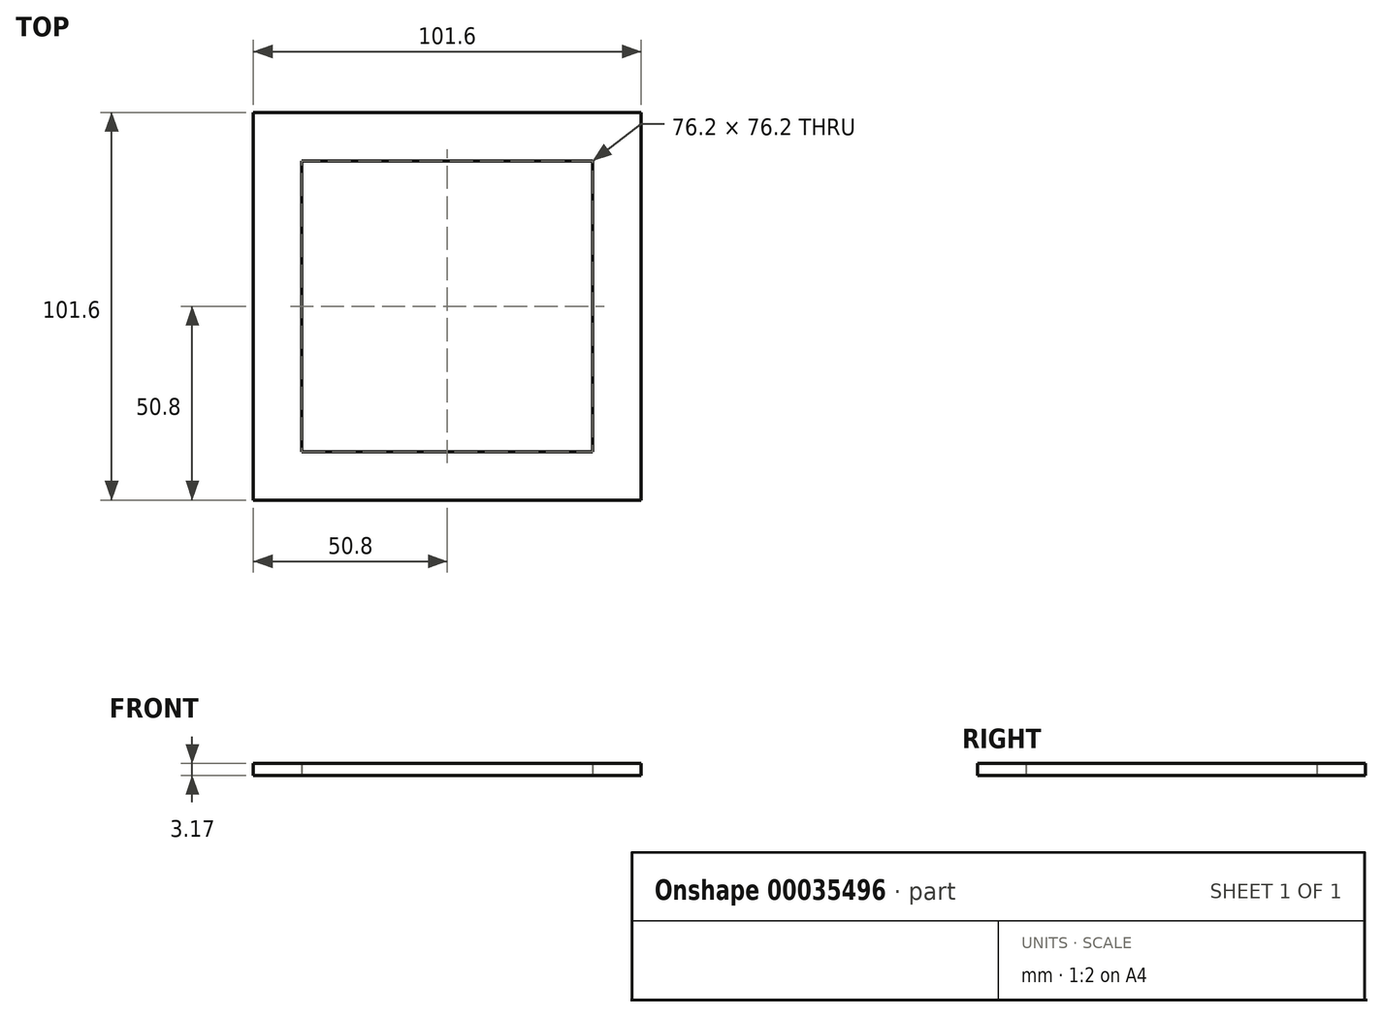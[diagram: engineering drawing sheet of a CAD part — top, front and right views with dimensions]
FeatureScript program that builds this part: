
annotation { "Feature Type Name" : "Feature", "Feature Type Description" : "" }
export const myFeature = defineFeature(function(context is Context, id is Id, definition is map)
    precondition{}
    {
        {
            var Q0;
            Q0=qCreatedBy(makeId("Top.planeOp"),FACE);
            var sketch = newSketch(context, id + "F0", { "sketchPlane" : qUnion([Q0])});
            skLineSegment(sketch, "E0.rect.bottom", {"start": v(-50.8, 50.8) * mm, "end": v(50.8, 50.8) * mm});
            skLineSegment(sketch, "E0.rect.top", {"start": v(-50.8, -50.8) * mm, "end": v(50.8, -50.8) * mm});
            skLineSegment(sketch, "E0.rect.left", {"start": v(-50.8, 50.8) * mm, "end": v(-50.8, -50.8) * mm});
            skLineSegment(sketch, "E0.rect.right", {"start": v(50.8, 50.8) * mm, "end": v(50.8, -50.8) * mm});
            skPoint(sketch, "E0.rect.middle", {"position": v(0, 0) * mm});
            skLineSegment(sketch, "E1.rect.bottom", {"start": v(-38.1, 38.1) * mm, "end": v(38.1, 38.1) * mm});
            skLineSegment(sketch, "E1.rect.top", {"start": v(-38.1, -38.1) * mm, "end": v(38.1, -38.1) * mm});
            skLineSegment(sketch, "E1.rect.left", {"start": v(-38.1, 38.1) * mm, "end": v(-38.1, -38.1) * mm});
            skLineSegment(sketch, "E1.rect.right", {"start": v(38.1, 38.1) * mm, "end": v(38.1, -38.1) * mm});
            skSolve(sketch);
        }
        {
            var Q0;
            Q0=makeQuery(id+"F0.imprint","IMPRINT",FACE,{"disambiguationData":[TD([[makeQuery(id+"F0.imprint","IMPRINT",EDGE,{"derivedFrom":sQuery(id+"F0.wireOp",EDGE,"E0.rect.bottom")}),-1.0]])]});
            extrude(context, id + "F1", {"entities" : qUnion([Q0]), "depth" : 3.17 * mm});
        }
    });
